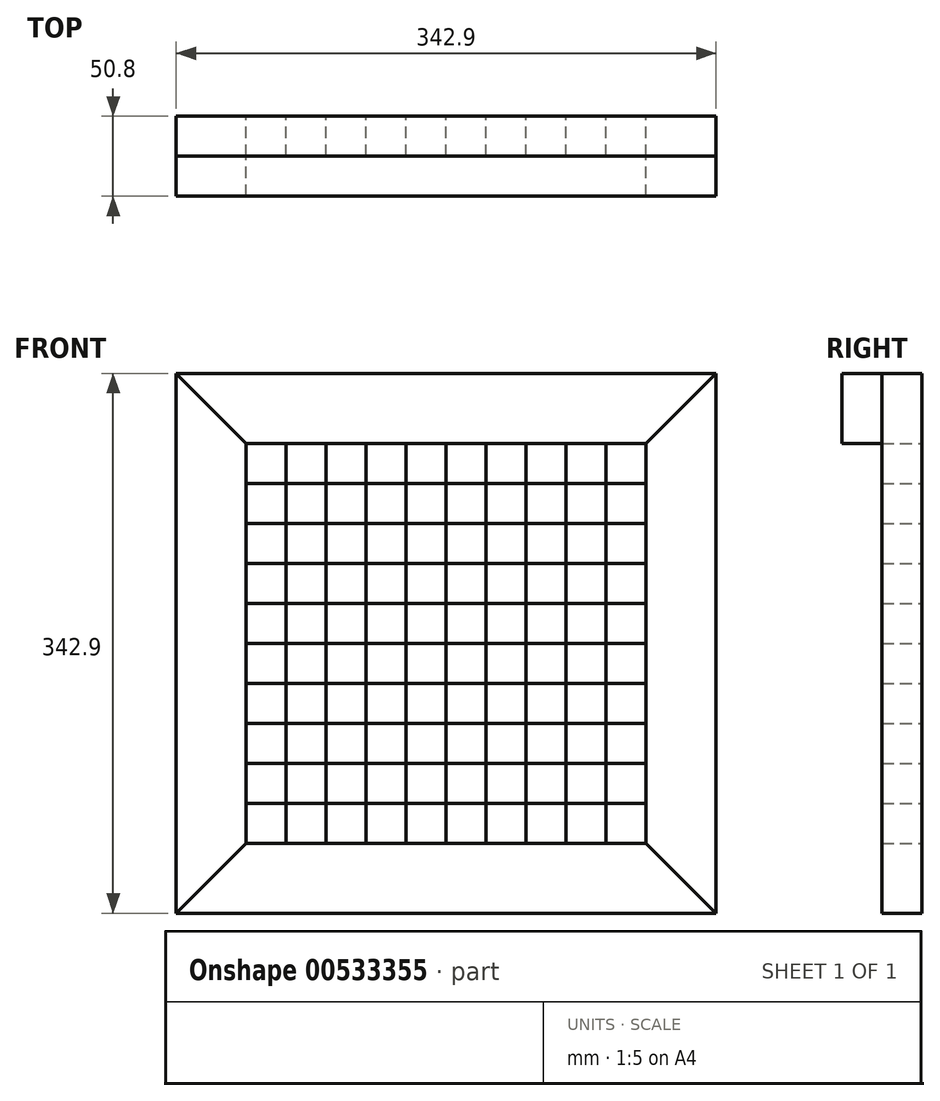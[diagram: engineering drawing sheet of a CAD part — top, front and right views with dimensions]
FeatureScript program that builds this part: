
annotation { "Feature Type Name" : "Feature", "Feature Type Description" : "" }
export const myFeature = defineFeature(function(context is Context, id is Id, definition is map)
    precondition{}
    {
        {
            var Q0;
            Q0=qCreatedBy(makeId("Front.planeOp"),FACE);
            var sketch = newSketch(context, id + "F0", { "sketchPlane" : qUnion([Q0])});
            skLineSegment(sketch, "E0.bottom", {"start": v(171.45, 171.45) * mm, "end": v(-171.45, 171.45) * mm});
            skLineSegment(sketch, "E0.top", {"start": v(171.45, -171.45) * mm, "end": v(-171.45, -171.45) * mm});
            skLineSegment(sketch, "E0.left", {"start": v(171.45, 171.45) * mm, "end": v(171.45, -171.45) * mm});
            skLineSegment(sketch, "E0.right", {"start": v(-171.45, 171.45) * mm, "end": v(-171.45, -171.45) * mm});
            skPoint(sketch, "E0.middle", {"position": v(0, 0) * mm});
            skLineSegment(sketch, "E1", {"start": v(-127, 127) * mm, "end": v(-127, -127) * mm});
            skLineSegment(sketch, "E2", {"start": v(127, 127) * mm, "end": v(127, -127) * mm});
            skLineSegment(sketch, "E3", {"start": v(-127, 127) * mm, "end": v(127, 127) * mm});
            skLineSegment(sketch, "E4", {"start": v(-127, -127) * mm, "end": v(127, -127) * mm});
            skLineSegment(sketch, "E5", {"start": v(-127, 127) * mm, "end": v(-171.45, 171.45) * mm});
            skLineSegment(sketch, "E6", {"start": v(127, 127) * mm, "end": v(171.45, 171.45) * mm});
            skLineSegment(sketch, "E7", {"start": v(127, -127) * mm, "end": v(171.45, -171.45) * mm});
            skLineSegment(sketch, "E8", {"start": v(-127, -127) * mm, "end": v(-171.45, -171.45) * mm});
            skLineSegment(sketch, "E9.0", {"start": v(-101.6, 127) * mm, "end": v(-101.6, -127) * mm});
            skLineSegment(sketch, "E10.0", {"start": v(-76.2, 127) * mm, "end": v(-76.2, -127) * mm});
            skLineSegment(sketch, "E11.0", {"start": v(-50.8, 127) * mm, "end": v(-50.8, -127) * mm});
            skLineSegment(sketch, "E12.0", {"start": v(-25.4, 127) * mm, "end": v(-25.4, -127) * mm});
            skLineSegment(sketch, "E13.0", {"start": v(0, 127) * mm, "end": v(0, -127) * mm});
            skLineSegment(sketch, "E14.0", {"start": v(25.4, 127) * mm, "end": v(25.4, -127) * mm});
            skLineSegment(sketch, "E15.0", {"start": v(50.8, 127) * mm, "end": v(50.8, -127) * mm});
            skLineSegment(sketch, "E16.0", {"start": v(76.2, 127) * mm, "end": v(76.2, -127) * mm});
            skLineSegment(sketch, "E17.0", {"start": v(101.6, 127) * mm, "end": v(101.6, -127) * mm});
            skLineSegment(sketch, "E18.0", {"start": v(-127, 101.6) * mm, "end": v(127, 101.6) * mm});
            skLineSegment(sketch, "E19.0", {"start": v(-127, 76.2) * mm, "end": v(127, 76.2) * mm});
            skLineSegment(sketch, "E20.0", {"start": v(-127, 50.8) * mm, "end": v(127, 50.8) * mm});
            skLineSegment(sketch, "E21.0", {"start": v(-127, 25.4) * mm, "end": v(127, 25.4) * mm});
            skLineSegment(sketch, "E22.0", {"start": v(-127, 0) * mm, "end": v(127, 0) * mm});
            skLineSegment(sketch, "E23.0", {"start": v(-127, -25.4) * mm, "end": v(127, -25.4) * mm});
            skLineSegment(sketch, "E24.0", {"start": v(-127, -50.8) * mm, "end": v(127, -50.8) * mm});
            skLineSegment(sketch, "E25.0", {"start": v(-127, -76.2) * mm, "end": v(127, -76.2) * mm});
            skLineSegment(sketch, "E26.0", {"start": v(-127, -101.6) * mm, "end": v(127, -101.6) * mm});
            skSolve(sketch);
        }
        {
            var Q0;
            Q0=makeQuery(id+"F0.imprint","IMPRINT",FACE,{"disambiguationData":[TD([[makeQuery(id+"F0.imprint","IMPRINT",EDGE,{"derivedFrom":sQuery(id+"F0.wireOp",EDGE,"E0.bottom")}),1.0]])]});
            extrude(context, id + "F1", {"entities" : qUnion([Q0]), "depth" : 25.4 * mm, "offsetDistance" : 25.4 * mm});
        }
        {
            var Q0;
            Q0=makeQuery(id+"F0.imprint","IMPRINT",FACE,{"disambiguationData":[TD([[makeQuery(id+"F0.imprint","IMPRINT",EDGE,{"derivedFrom":sQuery(id+"F0.wireOp",EDGE,"E0.right")}),1.0]])]});
            var Q1;
            Q1=makeQuery(id+"F0.imprint","IMPRINT",FACE,{"disambiguationData":[TD([[makeQuery(id+"F0.imprint","IMPRINT",EDGE,{"derivedFrom":sQuery(id+"F0.wireOp",EDGE,"E0.left")}),-1.0]])]});
            extrude(context, id + "F2", {"entities" : qUnion([Q0, Q1]), "depth" : 25.4 * mm, "offsetDistance" : 25.4 * mm});
        }
        {
            var Q0;
            Q0=makeQuery(id+"F0.imprint","IMPRINT",FACE,{"disambiguationData":[TD([[makeQuery(id+"F0.imprint","IMPRINT",EDGE,{"derivedFrom":sQuery(id+"F0.wireOp",EDGE,"E0.top")}),-1.0]])]});
            var Q1;
            Q1=makeQuery(id+"F1.opExtrude","CAP_FACE",FACE,{"disambiguationData":[OSD([sQuery(id+"F0.wireOp",EDGE,"E0.bottom"),sQuery(id+"F0.wireOp",EDGE,"E3"),sQuery(id+"F0.wireOp",EDGE,"E5"),sQuery(id+"F0.wireOp",EDGE,"E6")])],"isStart":false});
            extrude(context, id + "F3", {"entities" : qUnion([Q0, Q1]), "depth" : 25.4 * mm, "offsetDistance" : 25.4 * mm});
        }
        {
            var Q0;
            {var subQ0=sQuery(id+"F0.wireOp",EDGE,"E3");var subQ5=sQuery(id+"F0.wireOp",EDGE,"E9.0");var subQ6=makeQuery(id+"F0.imprint","INTERSECT",VERTEX,{"derivedFrom":[subQ0,subQ5]});Q0=makeQuery(id+"F0.imprint","IMPRINT",FACE,{"disambiguationData":[TD([[makeQuery(id+"F0.imprint","IMPRINT",EDGE,{"disambiguationData":[TD([[subQ6,-1.0]])],"derivedFrom":subQ5}),-1.0]])]});}
            var Q1;
            {var subQ0=sQuery(id+"F0.wireOp",EDGE,"E10.0");var subQ1=sQuery(id+"F0.wireOp",EDGE,"E3");var subQ2=makeQuery(id+"F0.imprint","INTERSECT",VERTEX,{"derivedFrom":[subQ1,subQ0]});Q1=makeQuery(id+"F0.imprint","IMPRINT",FACE,{"disambiguationData":[TD([[makeQuery(id+"F0.imprint","IMPRINT",EDGE,{"disambiguationData":[TD([[subQ2,-1.0]])],"derivedFrom":subQ1}),-1.0]])]});}
            var Q2;
            {var subQ0=sQuery(id+"F0.wireOp",EDGE,"E12.0");var subQ1=sQuery(id+"F0.wireOp",EDGE,"E3");var subQ2=makeQuery(id+"F0.imprint","INTERSECT",VERTEX,{"derivedFrom":[subQ1,subQ0]});Q2=makeQuery(id+"F0.imprint","IMPRINT",FACE,{"disambiguationData":[TD([[makeQuery(id+"F0.imprint","IMPRINT",EDGE,{"disambiguationData":[TD([[subQ2,-1.0]])],"derivedFrom":subQ1}),-1.0]])]});}
            var Q3;
            {var subQ0=sQuery(id+"F0.wireOp",EDGE,"E14.0");var subQ1=sQuery(id+"F0.wireOp",EDGE,"E3");var subQ2=makeQuery(id+"F0.imprint","INTERSECT",VERTEX,{"derivedFrom":[subQ1,subQ0]});Q3=makeQuery(id+"F0.imprint","IMPRINT",FACE,{"disambiguationData":[TD([[makeQuery(id+"F0.imprint","IMPRINT",EDGE,{"disambiguationData":[TD([[subQ2,-1.0]])],"derivedFrom":subQ1}),-1.0]])]});}
            var Q4;
            {var subQ0=sQuery(id+"F0.wireOp",EDGE,"E16.0");var subQ1=sQuery(id+"F0.wireOp",EDGE,"E3");var subQ2=makeQuery(id+"F0.imprint","INTERSECT",VERTEX,{"derivedFrom":[subQ1,subQ0]});Q4=makeQuery(id+"F0.imprint","IMPRINT",FACE,{"disambiguationData":[TD([[makeQuery(id+"F0.imprint","IMPRINT",EDGE,{"disambiguationData":[TD([[subQ2,-1.0]])],"derivedFrom":subQ1}),-1.0]])]});}
            var Q5;
            {var subQ0=sQuery(id+"F0.wireOp",EDGE,"E18.0");var subQ1=sQuery(id+"F0.wireOp",EDGE,"E9.0");var subQ2=makeQuery(id+"F0.imprint","INTERSECT",VERTEX,{"derivedFrom":[subQ1,subQ0]});Q5=makeQuery(id+"F0.imprint","IMPRINT",FACE,{"disambiguationData":[TD([[makeQuery(id+"F0.imprint","IMPRINT",EDGE,{"disambiguationData":[TD([[subQ2,-1.0]])],"derivedFrom":subQ1}),1.0]])]});}
            var Q6;
            {var subQ0=sQuery(id+"F0.wireOp",EDGE,"E18.0");var subQ1=sQuery(id+"F0.wireOp",EDGE,"E11.0");var subQ2=makeQuery(id+"F0.imprint","INTERSECT",VERTEX,{"derivedFrom":[subQ1,subQ0]});Q6=makeQuery(id+"F0.imprint","IMPRINT",FACE,{"disambiguationData":[TD([[makeQuery(id+"F0.imprint","IMPRINT",EDGE,{"disambiguationData":[TD([[subQ2,-1.0]])],"derivedFrom":subQ1}),1.0]])]});}
            var Q7;
            {var subQ0=sQuery(id+"F0.wireOp",EDGE,"E18.0");var subQ1=sQuery(id+"F0.wireOp",EDGE,"E13.0");var subQ2=makeQuery(id+"F0.imprint","INTERSECT",VERTEX,{"derivedFrom":[subQ1,subQ0]});Q7=makeQuery(id+"F0.imprint","IMPRINT",FACE,{"disambiguationData":[TD([[makeQuery(id+"F0.imprint","IMPRINT",EDGE,{"disambiguationData":[TD([[subQ2,-1.0]])],"derivedFrom":subQ1}),1.0]])]});}
            var Q8;
            {var subQ0=sQuery(id+"F0.wireOp",EDGE,"E18.0");var subQ1=sQuery(id+"F0.wireOp",EDGE,"E15.0");var subQ2=makeQuery(id+"F0.imprint","INTERSECT",VERTEX,{"derivedFrom":[subQ1,subQ0]});Q8=makeQuery(id+"F0.imprint","IMPRINT",FACE,{"disambiguationData":[TD([[makeQuery(id+"F0.imprint","IMPRINT",EDGE,{"disambiguationData":[TD([[subQ2,-1.0]])],"derivedFrom":subQ1}),1.0]])]});}
            var Q9;
            {var subQ0=sQuery(id+"F0.wireOp",EDGE,"E18.0");var subQ1=sQuery(id+"F0.wireOp",EDGE,"E2");var subQ2=makeQuery(id+"F0.imprint","INTERSECT",VERTEX,{"derivedFrom":[subQ1,subQ0]});Q9=makeQuery(id+"F0.imprint","IMPRINT",FACE,{"disambiguationData":[TD([[makeQuery(id+"F0.imprint","IMPRINT",EDGE,{"disambiguationData":[TD([[subQ2,-1.0]])],"derivedFrom":subQ1}),-1.0]])]});}
            var Q10;
            {var subQ0=sQuery(id+"F0.wireOp",EDGE,"E19.0");var subQ1=sQuery(id+"F0.wireOp",EDGE,"E16.0");var subQ2=makeQuery(id+"F0.imprint","INTERSECT",VERTEX,{"derivedFrom":[subQ1,subQ0]});Q10=makeQuery(id+"F0.imprint","IMPRINT",FACE,{"disambiguationData":[TD([[makeQuery(id+"F0.imprint","IMPRINT",EDGE,{"disambiguationData":[TD([[subQ2,-1.0]])],"derivedFrom":subQ1}),1.0]])]});}
            var Q11;
            {var subQ0=sQuery(id+"F0.wireOp",EDGE,"E19.0");var subQ1=sQuery(id+"F0.wireOp",EDGE,"E14.0");var subQ2=makeQuery(id+"F0.imprint","INTERSECT",VERTEX,{"derivedFrom":[subQ1,subQ0]});Q11=makeQuery(id+"F0.imprint","IMPRINT",FACE,{"disambiguationData":[TD([[makeQuery(id+"F0.imprint","IMPRINT",EDGE,{"disambiguationData":[TD([[subQ2,-1.0]])],"derivedFrom":subQ1}),1.0]])]});}
            var Q12;
            {var subQ0=sQuery(id+"F0.wireOp",EDGE,"E19.0");var subQ1=sQuery(id+"F0.wireOp",EDGE,"E12.0");var subQ2=makeQuery(id+"F0.imprint","INTERSECT",VERTEX,{"derivedFrom":[subQ1,subQ0]});Q12=makeQuery(id+"F0.imprint","IMPRINT",FACE,{"disambiguationData":[TD([[makeQuery(id+"F0.imprint","IMPRINT",EDGE,{"disambiguationData":[TD([[subQ2,-1.0]])],"derivedFrom":subQ1}),1.0]])]});}
            var Q13;
            {var subQ0=sQuery(id+"F0.wireOp",EDGE,"E19.0");var subQ1=sQuery(id+"F0.wireOp",EDGE,"E10.0");var subQ2=makeQuery(id+"F0.imprint","INTERSECT",VERTEX,{"derivedFrom":[subQ1,subQ0]});Q13=makeQuery(id+"F0.imprint","IMPRINT",FACE,{"disambiguationData":[TD([[makeQuery(id+"F0.imprint","IMPRINT",EDGE,{"disambiguationData":[TD([[subQ2,-1.0]])],"derivedFrom":subQ1}),1.0]])]});}
            var Q14;
            {var subQ0=sQuery(id+"F0.wireOp",EDGE,"E19.0");var subQ1=sQuery(id+"F0.wireOp",EDGE,"E1");var subQ2=makeQuery(id+"F0.imprint","INTERSECT",VERTEX,{"derivedFrom":[subQ1,subQ0]});Q14=makeQuery(id+"F0.imprint","IMPRINT",FACE,{"disambiguationData":[TD([[makeQuery(id+"F0.imprint","IMPRINT",EDGE,{"disambiguationData":[TD([[subQ2,-1.0]])],"derivedFrom":subQ1}),1.0]])]});}
            var Q15;
            {var subQ0=sQuery(id+"F0.wireOp",EDGE,"E20.0");var subQ1=sQuery(id+"F0.wireOp",EDGE,"E9.0");var subQ2=makeQuery(id+"F0.imprint","INTERSECT",VERTEX,{"derivedFrom":[subQ1,subQ0]});Q15=makeQuery(id+"F0.imprint","IMPRINT",FACE,{"disambiguationData":[TD([[makeQuery(id+"F0.imprint","IMPRINT",EDGE,{"disambiguationData":[TD([[subQ2,-1.0]])],"derivedFrom":subQ1}),1.0]])]});}
            var Q16;
            {var subQ0=sQuery(id+"F0.wireOp",EDGE,"E20.0");var subQ1=sQuery(id+"F0.wireOp",EDGE,"E11.0");var subQ2=makeQuery(id+"F0.imprint","INTERSECT",VERTEX,{"derivedFrom":[subQ1,subQ0]});Q16=makeQuery(id+"F0.imprint","IMPRINT",FACE,{"disambiguationData":[TD([[makeQuery(id+"F0.imprint","IMPRINT",EDGE,{"disambiguationData":[TD([[subQ2,-1.0]])],"derivedFrom":subQ1}),1.0]])]});}
            var Q17;
            {var subQ0=sQuery(id+"F0.wireOp",EDGE,"E20.0");var subQ1=sQuery(id+"F0.wireOp",EDGE,"E13.0");var subQ2=makeQuery(id+"F0.imprint","INTERSECT",VERTEX,{"derivedFrom":[subQ1,subQ0]});Q17=makeQuery(id+"F0.imprint","IMPRINT",FACE,{"disambiguationData":[TD([[makeQuery(id+"F0.imprint","IMPRINT",EDGE,{"disambiguationData":[TD([[subQ2,-1.0]])],"derivedFrom":subQ1}),1.0]])]});}
            var Q18;
            {var subQ0=sQuery(id+"F0.wireOp",EDGE,"E20.0");var subQ1=sQuery(id+"F0.wireOp",EDGE,"E15.0");var subQ2=makeQuery(id+"F0.imprint","INTERSECT",VERTEX,{"derivedFrom":[subQ1,subQ0]});Q18=makeQuery(id+"F0.imprint","IMPRINT",FACE,{"disambiguationData":[TD([[makeQuery(id+"F0.imprint","IMPRINT",EDGE,{"disambiguationData":[TD([[subQ2,-1.0]])],"derivedFrom":subQ1}),1.0]])]});}
            var Q19;
            {var subQ0=sQuery(id+"F0.wireOp",EDGE,"E20.0");var subQ1=sQuery(id+"F0.wireOp",EDGE,"E2");var subQ2=makeQuery(id+"F0.imprint","INTERSECT",VERTEX,{"derivedFrom":[subQ1,subQ0]});Q19=makeQuery(id+"F0.imprint","IMPRINT",FACE,{"disambiguationData":[TD([[makeQuery(id+"F0.imprint","IMPRINT",EDGE,{"disambiguationData":[TD([[subQ2,-1.0]])],"derivedFrom":subQ1}),-1.0]])]});}
            var Q20;
            {var subQ0=sQuery(id+"F0.wireOp",EDGE,"E21.0");var subQ1=sQuery(id+"F0.wireOp",EDGE,"E16.0");var subQ2=makeQuery(id+"F0.imprint","INTERSECT",VERTEX,{"derivedFrom":[subQ1,subQ0]});Q20=makeQuery(id+"F0.imprint","IMPRINT",FACE,{"disambiguationData":[TD([[makeQuery(id+"F0.imprint","IMPRINT",EDGE,{"disambiguationData":[TD([[subQ2,-1.0]])],"derivedFrom":subQ1}),1.0]])]});}
            var Q21;
            {var subQ0=sQuery(id+"F0.wireOp",EDGE,"E21.0");var subQ1=sQuery(id+"F0.wireOp",EDGE,"E14.0");var subQ2=makeQuery(id+"F0.imprint","INTERSECT",VERTEX,{"derivedFrom":[subQ1,subQ0]});Q21=makeQuery(id+"F0.imprint","IMPRINT",FACE,{"disambiguationData":[TD([[makeQuery(id+"F0.imprint","IMPRINT",EDGE,{"disambiguationData":[TD([[subQ2,-1.0]])],"derivedFrom":subQ1}),1.0]])]});}
            var Q22;
            {var subQ0=sQuery(id+"F0.wireOp",EDGE,"E21.0");var subQ1=sQuery(id+"F0.wireOp",EDGE,"E12.0");var subQ2=makeQuery(id+"F0.imprint","INTERSECT",VERTEX,{"derivedFrom":[subQ1,subQ0]});Q22=makeQuery(id+"F0.imprint","IMPRINT",FACE,{"disambiguationData":[TD([[makeQuery(id+"F0.imprint","IMPRINT",EDGE,{"disambiguationData":[TD([[subQ2,-1.0]])],"derivedFrom":subQ1}),1.0]])]});}
            var Q23;
            {var subQ0=sQuery(id+"F0.wireOp",EDGE,"E21.0");var subQ1=sQuery(id+"F0.wireOp",EDGE,"E10.0");var subQ2=makeQuery(id+"F0.imprint","INTERSECT",VERTEX,{"derivedFrom":[subQ1,subQ0]});Q23=makeQuery(id+"F0.imprint","IMPRINT",FACE,{"disambiguationData":[TD([[makeQuery(id+"F0.imprint","IMPRINT",EDGE,{"disambiguationData":[TD([[subQ2,-1.0]])],"derivedFrom":subQ1}),1.0]])]});}
            var Q24;
            {var subQ0=sQuery(id+"F0.wireOp",EDGE,"E21.0");var subQ1=sQuery(id+"F0.wireOp",EDGE,"E1");var subQ2=makeQuery(id+"F0.imprint","INTERSECT",VERTEX,{"derivedFrom":[subQ1,subQ0]});Q24=makeQuery(id+"F0.imprint","IMPRINT",FACE,{"disambiguationData":[TD([[makeQuery(id+"F0.imprint","IMPRINT",EDGE,{"disambiguationData":[TD([[subQ2,-1.0]])],"derivedFrom":subQ1}),1.0]])]});}
            var Q25;
            {var subQ0=sQuery(id+"F0.wireOp",EDGE,"E22.0");var subQ1=sQuery(id+"F0.wireOp",EDGE,"E9.0");var subQ2=makeQuery(id+"F0.imprint","INTERSECT",VERTEX,{"derivedFrom":[subQ1,subQ0]});Q25=makeQuery(id+"F0.imprint","IMPRINT",FACE,{"disambiguationData":[TD([[makeQuery(id+"F0.imprint","IMPRINT",EDGE,{"disambiguationData":[TD([[subQ2,-1.0]])],"derivedFrom":subQ1}),1.0]])]});}
            var Q26;
            {var subQ0=sQuery(id+"F0.wireOp",EDGE,"E22.0");var subQ1=sQuery(id+"F0.wireOp",EDGE,"E11.0");var subQ2=makeQuery(id+"F0.imprint","INTERSECT",VERTEX,{"derivedFrom":[subQ1,subQ0]});Q26=makeQuery(id+"F0.imprint","IMPRINT",FACE,{"disambiguationData":[TD([[makeQuery(id+"F0.imprint","IMPRINT",EDGE,{"disambiguationData":[TD([[subQ2,-1.0]])],"derivedFrom":subQ1}),1.0]])]});}
            var Q27;
            {var subQ0=sQuery(id+"F0.wireOp",EDGE,"E22.0");var subQ1=sQuery(id+"F0.wireOp",EDGE,"E13.0");var subQ2=makeQuery(id+"F0.imprint","INTERSECT",VERTEX,{"derivedFrom":[subQ1,subQ0]});Q27=makeQuery(id+"F0.imprint","IMPRINT",FACE,{"disambiguationData":[TD([[makeQuery(id+"F0.imprint","IMPRINT",EDGE,{"disambiguationData":[TD([[subQ2,-1.0]])],"derivedFrom":subQ1}),1.0]])]});}
            var Q28;
            {var subQ0=sQuery(id+"F0.wireOp",EDGE,"E22.0");var subQ1=sQuery(id+"F0.wireOp",EDGE,"E15.0");var subQ2=makeQuery(id+"F0.imprint","INTERSECT",VERTEX,{"derivedFrom":[subQ1,subQ0]});Q28=makeQuery(id+"F0.imprint","IMPRINT",FACE,{"disambiguationData":[TD([[makeQuery(id+"F0.imprint","IMPRINT",EDGE,{"disambiguationData":[TD([[subQ2,-1.0]])],"derivedFrom":subQ1}),1.0]])]});}
            var Q29;
            {var subQ0=sQuery(id+"F0.wireOp",EDGE,"E22.0");var subQ1=sQuery(id+"F0.wireOp",EDGE,"E2");var subQ2=makeQuery(id+"F0.imprint","INTERSECT",VERTEX,{"derivedFrom":[subQ1,subQ0]});Q29=makeQuery(id+"F0.imprint","IMPRINT",FACE,{"disambiguationData":[TD([[makeQuery(id+"F0.imprint","IMPRINT",EDGE,{"disambiguationData":[TD([[subQ2,-1.0]])],"derivedFrom":subQ1}),-1.0]])]});}
            var Q30;
            {var subQ0=sQuery(id+"F0.wireOp",EDGE,"E23.0");var subQ1=sQuery(id+"F0.wireOp",EDGE,"E16.0");var subQ2=makeQuery(id+"F0.imprint","INTERSECT",VERTEX,{"derivedFrom":[subQ1,subQ0]});Q30=makeQuery(id+"F0.imprint","IMPRINT",FACE,{"disambiguationData":[TD([[makeQuery(id+"F0.imprint","IMPRINT",EDGE,{"disambiguationData":[TD([[subQ2,-1.0]])],"derivedFrom":subQ1}),1.0]])]});}
            var Q31;
            {var subQ0=sQuery(id+"F0.wireOp",EDGE,"E23.0");var subQ1=sQuery(id+"F0.wireOp",EDGE,"E14.0");var subQ2=makeQuery(id+"F0.imprint","INTERSECT",VERTEX,{"derivedFrom":[subQ1,subQ0]});Q31=makeQuery(id+"F0.imprint","IMPRINT",FACE,{"disambiguationData":[TD([[makeQuery(id+"F0.imprint","IMPRINT",EDGE,{"disambiguationData":[TD([[subQ2,-1.0]])],"derivedFrom":subQ1}),1.0]])]});}
            var Q32;
            {var subQ0=sQuery(id+"F0.wireOp",EDGE,"E23.0");var subQ1=sQuery(id+"F0.wireOp",EDGE,"E12.0");var subQ2=makeQuery(id+"F0.imprint","INTERSECT",VERTEX,{"derivedFrom":[subQ1,subQ0]});Q32=makeQuery(id+"F0.imprint","IMPRINT",FACE,{"disambiguationData":[TD([[makeQuery(id+"F0.imprint","IMPRINT",EDGE,{"disambiguationData":[TD([[subQ2,-1.0]])],"derivedFrom":subQ1}),1.0]])]});}
            var Q33;
            {var subQ0=sQuery(id+"F0.wireOp",EDGE,"E23.0");var subQ1=sQuery(id+"F0.wireOp",EDGE,"E10.0");var subQ2=makeQuery(id+"F0.imprint","INTERSECT",VERTEX,{"derivedFrom":[subQ1,subQ0]});Q33=makeQuery(id+"F0.imprint","IMPRINT",FACE,{"disambiguationData":[TD([[makeQuery(id+"F0.imprint","IMPRINT",EDGE,{"disambiguationData":[TD([[subQ2,-1.0]])],"derivedFrom":subQ1}),1.0]])]});}
            var Q34;
            {var subQ0=sQuery(id+"F0.wireOp",EDGE,"E23.0");var subQ1=sQuery(id+"F0.wireOp",EDGE,"E1");var subQ2=makeQuery(id+"F0.imprint","INTERSECT",VERTEX,{"derivedFrom":[subQ1,subQ0]});Q34=makeQuery(id+"F0.imprint","IMPRINT",FACE,{"disambiguationData":[TD([[makeQuery(id+"F0.imprint","IMPRINT",EDGE,{"disambiguationData":[TD([[subQ2,-1.0]])],"derivedFrom":subQ1}),1.0]])]});}
            var Q35;
            {var subQ0=sQuery(id+"F0.wireOp",EDGE,"E24.0");var subQ1=sQuery(id+"F0.wireOp",EDGE,"E9.0");var subQ2=makeQuery(id+"F0.imprint","INTERSECT",VERTEX,{"derivedFrom":[subQ1,subQ0]});Q35=makeQuery(id+"F0.imprint","IMPRINT",FACE,{"disambiguationData":[TD([[makeQuery(id+"F0.imprint","IMPRINT",EDGE,{"disambiguationData":[TD([[subQ2,-1.0]])],"derivedFrom":subQ1}),1.0]])]});}
            var Q36;
            {var subQ0=sQuery(id+"F0.wireOp",EDGE,"E24.0");var subQ1=sQuery(id+"F0.wireOp",EDGE,"E11.0");var subQ2=makeQuery(id+"F0.imprint","INTERSECT",VERTEX,{"derivedFrom":[subQ1,subQ0]});Q36=makeQuery(id+"F0.imprint","IMPRINT",FACE,{"disambiguationData":[TD([[makeQuery(id+"F0.imprint","IMPRINT",EDGE,{"disambiguationData":[TD([[subQ2,-1.0]])],"derivedFrom":subQ1}),1.0]])]});}
            var Q37;
            {var subQ0=sQuery(id+"F0.wireOp",EDGE,"E24.0");var subQ1=sQuery(id+"F0.wireOp",EDGE,"E13.0");var subQ2=makeQuery(id+"F0.imprint","INTERSECT",VERTEX,{"derivedFrom":[subQ1,subQ0]});Q37=makeQuery(id+"F0.imprint","IMPRINT",FACE,{"disambiguationData":[TD([[makeQuery(id+"F0.imprint","IMPRINT",EDGE,{"disambiguationData":[TD([[subQ2,-1.0]])],"derivedFrom":subQ1}),1.0]])]});}
            var Q38;
            {var subQ0=sQuery(id+"F0.wireOp",EDGE,"E24.0");var subQ1=sQuery(id+"F0.wireOp",EDGE,"E15.0");var subQ2=makeQuery(id+"F0.imprint","INTERSECT",VERTEX,{"derivedFrom":[subQ1,subQ0]});Q38=makeQuery(id+"F0.imprint","IMPRINT",FACE,{"disambiguationData":[TD([[makeQuery(id+"F0.imprint","IMPRINT",EDGE,{"disambiguationData":[TD([[subQ2,-1.0]])],"derivedFrom":subQ1}),1.0]])]});}
            var Q39;
            {var subQ0=sQuery(id+"F0.wireOp",EDGE,"E24.0");var subQ1=sQuery(id+"F0.wireOp",EDGE,"E2");var subQ2=makeQuery(id+"F0.imprint","INTERSECT",VERTEX,{"derivedFrom":[subQ1,subQ0]});Q39=makeQuery(id+"F0.imprint","IMPRINT",FACE,{"disambiguationData":[TD([[makeQuery(id+"F0.imprint","IMPRINT",EDGE,{"disambiguationData":[TD([[subQ2,-1.0]])],"derivedFrom":subQ1}),-1.0]])]});}
            var Q40;
            {var subQ0=sQuery(id+"F0.wireOp",EDGE,"E25.0");var subQ1=sQuery(id+"F0.wireOp",EDGE,"E16.0");var subQ2=makeQuery(id+"F0.imprint","INTERSECT",VERTEX,{"derivedFrom":[subQ1,subQ0]});Q40=makeQuery(id+"F0.imprint","IMPRINT",FACE,{"disambiguationData":[TD([[makeQuery(id+"F0.imprint","IMPRINT",EDGE,{"disambiguationData":[TD([[subQ2,-1.0]])],"derivedFrom":subQ1}),1.0]])]});}
            var Q41;
            {var subQ0=sQuery(id+"F0.wireOp",EDGE,"E25.0");var subQ1=sQuery(id+"F0.wireOp",EDGE,"E14.0");var subQ2=makeQuery(id+"F0.imprint","INTERSECT",VERTEX,{"derivedFrom":[subQ1,subQ0]});Q41=makeQuery(id+"F0.imprint","IMPRINT",FACE,{"disambiguationData":[TD([[makeQuery(id+"F0.imprint","IMPRINT",EDGE,{"disambiguationData":[TD([[subQ2,-1.0]])],"derivedFrom":subQ1}),1.0]])]});}
            var Q42;
            {var subQ0=sQuery(id+"F0.wireOp",EDGE,"E25.0");var subQ1=sQuery(id+"F0.wireOp",EDGE,"E12.0");var subQ2=makeQuery(id+"F0.imprint","INTERSECT",VERTEX,{"derivedFrom":[subQ1,subQ0]});Q42=makeQuery(id+"F0.imprint","IMPRINT",FACE,{"disambiguationData":[TD([[makeQuery(id+"F0.imprint","IMPRINT",EDGE,{"disambiguationData":[TD([[subQ2,-1.0]])],"derivedFrom":subQ1}),1.0]])]});}
            var Q43;
            {var subQ0=sQuery(id+"F0.wireOp",EDGE,"E25.0");var subQ1=sQuery(id+"F0.wireOp",EDGE,"E10.0");var subQ2=makeQuery(id+"F0.imprint","INTERSECT",VERTEX,{"derivedFrom":[subQ1,subQ0]});Q43=makeQuery(id+"F0.imprint","IMPRINT",FACE,{"disambiguationData":[TD([[makeQuery(id+"F0.imprint","IMPRINT",EDGE,{"disambiguationData":[TD([[subQ2,-1.0]])],"derivedFrom":subQ1}),1.0]])]});}
            var Q44;
            {var subQ0=sQuery(id+"F0.wireOp",EDGE,"E25.0");var subQ1=sQuery(id+"F0.wireOp",EDGE,"E1");var subQ2=makeQuery(id+"F0.imprint","INTERSECT",VERTEX,{"derivedFrom":[subQ1,subQ0]});Q44=makeQuery(id+"F0.imprint","IMPRINT",FACE,{"disambiguationData":[TD([[makeQuery(id+"F0.imprint","IMPRINT",EDGE,{"disambiguationData":[TD([[subQ2,-1.0]])],"derivedFrom":subQ1}),1.0]])]});}
            var Q45;
            {var subQ0=sQuery(id+"F0.wireOp",EDGE,"E9.0");var subQ1=sQuery(id+"F0.wireOp",EDGE,"E4");var subQ2=makeQuery(id+"F0.imprint","INTERSECT",VERTEX,{"derivedFrom":[subQ1,subQ0]});Q45=makeQuery(id+"F0.imprint","IMPRINT",FACE,{"disambiguationData":[TD([[makeQuery(id+"F0.imprint","IMPRINT",EDGE,{"disambiguationData":[TD([[subQ2,-1.0]])],"derivedFrom":subQ1}),1.0]])]});}
            var Q46;
            {var subQ0=sQuery(id+"F0.wireOp",EDGE,"E13.0");var subQ1=sQuery(id+"F0.wireOp",EDGE,"E4");var subQ2=makeQuery(id+"F0.imprint","INTERSECT",VERTEX,{"derivedFrom":[subQ1,subQ0]});Q46=makeQuery(id+"F0.imprint","IMPRINT",FACE,{"disambiguationData":[TD([[makeQuery(id+"F0.imprint","IMPRINT",EDGE,{"disambiguationData":[TD([[subQ2,-1.0]])],"derivedFrom":subQ1}),1.0]])]});}
            var Q47;
            {var subQ0=sQuery(id+"F0.wireOp",EDGE,"E11.0");var subQ1=sQuery(id+"F0.wireOp",EDGE,"E4");var subQ2=makeQuery(id+"F0.imprint","INTERSECT",VERTEX,{"derivedFrom":[subQ1,subQ0]});Q47=makeQuery(id+"F0.imprint","IMPRINT",FACE,{"disambiguationData":[TD([[makeQuery(id+"F0.imprint","IMPRINT",EDGE,{"disambiguationData":[TD([[subQ2,-1.0]])],"derivedFrom":subQ1}),1.0]])]});}
            var Q48;
            {var subQ0=sQuery(id+"F0.wireOp",EDGE,"E15.0");var subQ1=sQuery(id+"F0.wireOp",EDGE,"E4");var subQ2=makeQuery(id+"F0.imprint","INTERSECT",VERTEX,{"derivedFrom":[subQ1,subQ0]});Q48=makeQuery(id+"F0.imprint","IMPRINT",FACE,{"disambiguationData":[TD([[makeQuery(id+"F0.imprint","IMPRINT",EDGE,{"disambiguationData":[TD([[subQ2,-1.0]])],"derivedFrom":subQ1}),1.0]])]});}
            var Q49;
            {var subQ0=sQuery(id+"F0.wireOp",EDGE,"E4");var subQ5=sQuery(id+"F0.wireOp",EDGE,"E17.0");var subQ6=makeQuery(id+"F0.imprint","INTERSECT",VERTEX,{"derivedFrom":[subQ0,subQ5]});Q49=makeQuery(id+"F0.imprint","IMPRINT",FACE,{"disambiguationData":[TD([[makeQuery(id+"F0.imprint","IMPRINT",EDGE,{"disambiguationData":[TD([[subQ6,1.0]])],"derivedFrom":subQ5}),1.0]])]});}
            extrude(context, id + "F4", {"entities" : qUnion([Q0, Q1, Q2, Q3, Q4, Q5, Q6, Q7, Q8, Q9, Q10, Q11, Q12, Q13, Q14, Q15, Q16, Q17, Q18, Q19, Q20, Q21, Q22, Q23, Q24, Q25, Q26, Q27, Q28, Q29, Q30, Q31, Q32, Q33, Q34, Q35, Q36, Q37, Q38, Q39, Q40, Q41, Q42, Q43, Q44, Q45, Q46, Q47, Q48, Q49]), "depth" : 25.4 * mm, "offsetDistance" : 25.4 * mm});
        }
        {
            var Q0;
            {var subQ0=sQuery(id+"F0.wireOp",EDGE,"E9.0");var subQ1=sQuery(id+"F0.wireOp",EDGE,"E3");var subQ2=makeQuery(id+"F0.imprint","INTERSECT",VERTEX,{"derivedFrom":[subQ1,subQ0]});Q0=makeQuery(id+"F0.imprint","IMPRINT",FACE,{"disambiguationData":[TD([[makeQuery(id+"F0.imprint","IMPRINT",EDGE,{"disambiguationData":[TD([[subQ2,-1.0]])],"derivedFrom":subQ1}),-1.0]])]});}
            var Q1;
            {var subQ0=sQuery(id+"F0.wireOp",EDGE,"E11.0");var subQ1=sQuery(id+"F0.wireOp",EDGE,"E3");var subQ2=makeQuery(id+"F0.imprint","INTERSECT",VERTEX,{"derivedFrom":[subQ1,subQ0]});Q1=makeQuery(id+"F0.imprint","IMPRINT",FACE,{"disambiguationData":[TD([[makeQuery(id+"F0.imprint","IMPRINT",EDGE,{"disambiguationData":[TD([[subQ2,-1.0]])],"derivedFrom":subQ1}),-1.0]])]});}
            var Q2;
            {var subQ0=sQuery(id+"F0.wireOp",EDGE,"E13.0");var subQ1=sQuery(id+"F0.wireOp",EDGE,"E3");var subQ2=makeQuery(id+"F0.imprint","INTERSECT",VERTEX,{"derivedFrom":[subQ1,subQ0]});Q2=makeQuery(id+"F0.imprint","IMPRINT",FACE,{"disambiguationData":[TD([[makeQuery(id+"F0.imprint","IMPRINT",EDGE,{"disambiguationData":[TD([[subQ2,-1.0]])],"derivedFrom":subQ1}),-1.0]])]});}
            var Q3;
            {var subQ0=sQuery(id+"F0.wireOp",EDGE,"E15.0");var subQ1=sQuery(id+"F0.wireOp",EDGE,"E3");var subQ2=makeQuery(id+"F0.imprint","INTERSECT",VERTEX,{"derivedFrom":[subQ1,subQ0]});Q3=makeQuery(id+"F0.imprint","IMPRINT",FACE,{"disambiguationData":[TD([[makeQuery(id+"F0.imprint","IMPRINT",EDGE,{"disambiguationData":[TD([[subQ2,-1.0]])],"derivedFrom":subQ1}),-1.0]])]});}
            var Q4;
            {var subQ0=sQuery(id+"F0.wireOp",EDGE,"E3");var subQ5=sQuery(id+"F0.wireOp",EDGE,"E17.0");var subQ6=makeQuery(id+"F0.imprint","INTERSECT",VERTEX,{"derivedFrom":[subQ0,subQ5]});Q4=makeQuery(id+"F0.imprint","IMPRINT",FACE,{"disambiguationData":[TD([[makeQuery(id+"F0.imprint","IMPRINT",EDGE,{"disambiguationData":[TD([[subQ6,-1.0]])],"derivedFrom":subQ5}),1.0]])]});}
            var Q5;
            {var subQ0=sQuery(id+"F0.wireOp",EDGE,"E18.0");var subQ1=sQuery(id+"F0.wireOp",EDGE,"E16.0");var subQ2=makeQuery(id+"F0.imprint","INTERSECT",VERTEX,{"derivedFrom":[subQ1,subQ0]});Q5=makeQuery(id+"F0.imprint","IMPRINT",FACE,{"disambiguationData":[TD([[makeQuery(id+"F0.imprint","IMPRINT",EDGE,{"disambiguationData":[TD([[subQ2,-1.0]])],"derivedFrom":subQ1}),1.0]])]});}
            var Q6;
            {var subQ0=sQuery(id+"F0.wireOp",EDGE,"E18.0");var subQ1=sQuery(id+"F0.wireOp",EDGE,"E14.0");var subQ2=makeQuery(id+"F0.imprint","INTERSECT",VERTEX,{"derivedFrom":[subQ1,subQ0]});Q6=makeQuery(id+"F0.imprint","IMPRINT",FACE,{"disambiguationData":[TD([[makeQuery(id+"F0.imprint","IMPRINT",EDGE,{"disambiguationData":[TD([[subQ2,-1.0]])],"derivedFrom":subQ1}),1.0]])]});}
            var Q7;
            {var subQ0=sQuery(id+"F0.wireOp",EDGE,"E18.0");var subQ1=sQuery(id+"F0.wireOp",EDGE,"E12.0");var subQ2=makeQuery(id+"F0.imprint","INTERSECT",VERTEX,{"derivedFrom":[subQ1,subQ0]});Q7=makeQuery(id+"F0.imprint","IMPRINT",FACE,{"disambiguationData":[TD([[makeQuery(id+"F0.imprint","IMPRINT",EDGE,{"disambiguationData":[TD([[subQ2,-1.0]])],"derivedFrom":subQ1}),1.0]])]});}
            var Q8;
            {var subQ0=sQuery(id+"F0.wireOp",EDGE,"E18.0");var subQ1=sQuery(id+"F0.wireOp",EDGE,"E10.0");var subQ2=makeQuery(id+"F0.imprint","INTERSECT",VERTEX,{"derivedFrom":[subQ1,subQ0]});Q8=makeQuery(id+"F0.imprint","IMPRINT",FACE,{"disambiguationData":[TD([[makeQuery(id+"F0.imprint","IMPRINT",EDGE,{"disambiguationData":[TD([[subQ2,-1.0]])],"derivedFrom":subQ1}),1.0]])]});}
            var Q9;
            {var subQ0=sQuery(id+"F0.wireOp",EDGE,"E18.0");var subQ1=sQuery(id+"F0.wireOp",EDGE,"E1");var subQ2=makeQuery(id+"F0.imprint","INTERSECT",VERTEX,{"derivedFrom":[subQ1,subQ0]});Q9=makeQuery(id+"F0.imprint","IMPRINT",FACE,{"disambiguationData":[TD([[makeQuery(id+"F0.imprint","IMPRINT",EDGE,{"disambiguationData":[TD([[subQ2,-1.0]])],"derivedFrom":subQ1}),1.0]])]});}
            var Q10;
            {var subQ0=sQuery(id+"F0.wireOp",EDGE,"E19.0");var subQ1=sQuery(id+"F0.wireOp",EDGE,"E9.0");var subQ2=makeQuery(id+"F0.imprint","INTERSECT",VERTEX,{"derivedFrom":[subQ1,subQ0]});Q10=makeQuery(id+"F0.imprint","IMPRINT",FACE,{"disambiguationData":[TD([[makeQuery(id+"F0.imprint","IMPRINT",EDGE,{"disambiguationData":[TD([[subQ2,-1.0]])],"derivedFrom":subQ1}),1.0]])]});}
            var Q11;
            {var subQ0=sQuery(id+"F0.wireOp",EDGE,"E19.0");var subQ1=sQuery(id+"F0.wireOp",EDGE,"E11.0");var subQ2=makeQuery(id+"F0.imprint","INTERSECT",VERTEX,{"derivedFrom":[subQ1,subQ0]});Q11=makeQuery(id+"F0.imprint","IMPRINT",FACE,{"disambiguationData":[TD([[makeQuery(id+"F0.imprint","IMPRINT",EDGE,{"disambiguationData":[TD([[subQ2,-1.0]])],"derivedFrom":subQ1}),1.0]])]});}
            var Q12;
            {var subQ0=sQuery(id+"F0.wireOp",EDGE,"E19.0");var subQ1=sQuery(id+"F0.wireOp",EDGE,"E13.0");var subQ2=makeQuery(id+"F0.imprint","INTERSECT",VERTEX,{"derivedFrom":[subQ1,subQ0]});Q12=makeQuery(id+"F0.imprint","IMPRINT",FACE,{"disambiguationData":[TD([[makeQuery(id+"F0.imprint","IMPRINT",EDGE,{"disambiguationData":[TD([[subQ2,-1.0]])],"derivedFrom":subQ1}),1.0]])]});}
            var Q13;
            {var subQ0=sQuery(id+"F0.wireOp",EDGE,"E19.0");var subQ1=sQuery(id+"F0.wireOp",EDGE,"E15.0");var subQ2=makeQuery(id+"F0.imprint","INTERSECT",VERTEX,{"derivedFrom":[subQ1,subQ0]});Q13=makeQuery(id+"F0.imprint","IMPRINT",FACE,{"disambiguationData":[TD([[makeQuery(id+"F0.imprint","IMPRINT",EDGE,{"disambiguationData":[TD([[subQ2,-1.0]])],"derivedFrom":subQ1}),1.0]])]});}
            var Q14;
            {var subQ0=sQuery(id+"F0.wireOp",EDGE,"E19.0");var subQ1=sQuery(id+"F0.wireOp",EDGE,"E2");var subQ2=makeQuery(id+"F0.imprint","INTERSECT",VERTEX,{"derivedFrom":[subQ1,subQ0]});Q14=makeQuery(id+"F0.imprint","IMPRINT",FACE,{"disambiguationData":[TD([[makeQuery(id+"F0.imprint","IMPRINT",EDGE,{"disambiguationData":[TD([[subQ2,-1.0]])],"derivedFrom":subQ1}),-1.0]])]});}
            var Q15;
            {var subQ0=sQuery(id+"F0.wireOp",EDGE,"E20.0");var subQ1=sQuery(id+"F0.wireOp",EDGE,"E16.0");var subQ2=makeQuery(id+"F0.imprint","INTERSECT",VERTEX,{"derivedFrom":[subQ1,subQ0]});Q15=makeQuery(id+"F0.imprint","IMPRINT",FACE,{"disambiguationData":[TD([[makeQuery(id+"F0.imprint","IMPRINT",EDGE,{"disambiguationData":[TD([[subQ2,-1.0]])],"derivedFrom":subQ1}),1.0]])]});}
            var Q16;
            {var subQ0=sQuery(id+"F0.wireOp",EDGE,"E20.0");var subQ1=sQuery(id+"F0.wireOp",EDGE,"E14.0");var subQ2=makeQuery(id+"F0.imprint","INTERSECT",VERTEX,{"derivedFrom":[subQ1,subQ0]});Q16=makeQuery(id+"F0.imprint","IMPRINT",FACE,{"disambiguationData":[TD([[makeQuery(id+"F0.imprint","IMPRINT",EDGE,{"disambiguationData":[TD([[subQ2,-1.0]])],"derivedFrom":subQ1}),1.0]])]});}
            var Q17;
            {var subQ0=sQuery(id+"F0.wireOp",EDGE,"E20.0");var subQ1=sQuery(id+"F0.wireOp",EDGE,"E12.0");var subQ2=makeQuery(id+"F0.imprint","INTERSECT",VERTEX,{"derivedFrom":[subQ1,subQ0]});Q17=makeQuery(id+"F0.imprint","IMPRINT",FACE,{"disambiguationData":[TD([[makeQuery(id+"F0.imprint","IMPRINT",EDGE,{"disambiguationData":[TD([[subQ2,-1.0]])],"derivedFrom":subQ1}),1.0]])]});}
            var Q18;
            {var subQ0=sQuery(id+"F0.wireOp",EDGE,"E20.0");var subQ1=sQuery(id+"F0.wireOp",EDGE,"E10.0");var subQ2=makeQuery(id+"F0.imprint","INTERSECT",VERTEX,{"derivedFrom":[subQ1,subQ0]});Q18=makeQuery(id+"F0.imprint","IMPRINT",FACE,{"disambiguationData":[TD([[makeQuery(id+"F0.imprint","IMPRINT",EDGE,{"disambiguationData":[TD([[subQ2,-1.0]])],"derivedFrom":subQ1}),1.0]])]});}
            var Q19;
            {var subQ0=sQuery(id+"F0.wireOp",EDGE,"E20.0");var subQ1=sQuery(id+"F0.wireOp",EDGE,"E1");var subQ2=makeQuery(id+"F0.imprint","INTERSECT",VERTEX,{"derivedFrom":[subQ1,subQ0]});Q19=makeQuery(id+"F0.imprint","IMPRINT",FACE,{"disambiguationData":[TD([[makeQuery(id+"F0.imprint","IMPRINT",EDGE,{"disambiguationData":[TD([[subQ2,-1.0]])],"derivedFrom":subQ1}),1.0]])]});}
            var Q20;
            {var subQ0=sQuery(id+"F0.wireOp",EDGE,"E21.0");var subQ1=sQuery(id+"F0.wireOp",EDGE,"E9.0");var subQ2=makeQuery(id+"F0.imprint","INTERSECT",VERTEX,{"derivedFrom":[subQ1,subQ0]});Q20=makeQuery(id+"F0.imprint","IMPRINT",FACE,{"disambiguationData":[TD([[makeQuery(id+"F0.imprint","IMPRINT",EDGE,{"disambiguationData":[TD([[subQ2,-1.0]])],"derivedFrom":subQ1}),1.0]])]});}
            var Q21;
            {var subQ0=sQuery(id+"F0.wireOp",EDGE,"E21.0");var subQ1=sQuery(id+"F0.wireOp",EDGE,"E11.0");var subQ2=makeQuery(id+"F0.imprint","INTERSECT",VERTEX,{"derivedFrom":[subQ1,subQ0]});Q21=makeQuery(id+"F0.imprint","IMPRINT",FACE,{"disambiguationData":[TD([[makeQuery(id+"F0.imprint","IMPRINT",EDGE,{"disambiguationData":[TD([[subQ2,-1.0]])],"derivedFrom":subQ1}),1.0]])]});}
            var Q22;
            {var subQ0=sQuery(id+"F0.wireOp",EDGE,"E21.0");var subQ1=sQuery(id+"F0.wireOp",EDGE,"E13.0");var subQ2=makeQuery(id+"F0.imprint","INTERSECT",VERTEX,{"derivedFrom":[subQ1,subQ0]});Q22=makeQuery(id+"F0.imprint","IMPRINT",FACE,{"disambiguationData":[TD([[makeQuery(id+"F0.imprint","IMPRINT",EDGE,{"disambiguationData":[TD([[subQ2,-1.0]])],"derivedFrom":subQ1}),1.0]])]});}
            var Q23;
            {var subQ0=sQuery(id+"F0.wireOp",EDGE,"E21.0");var subQ1=sQuery(id+"F0.wireOp",EDGE,"E15.0");var subQ2=makeQuery(id+"F0.imprint","INTERSECT",VERTEX,{"derivedFrom":[subQ1,subQ0]});Q23=makeQuery(id+"F0.imprint","IMPRINT",FACE,{"disambiguationData":[TD([[makeQuery(id+"F0.imprint","IMPRINT",EDGE,{"disambiguationData":[TD([[subQ2,-1.0]])],"derivedFrom":subQ1}),1.0]])]});}
            var Q24;
            {var subQ0=sQuery(id+"F0.wireOp",EDGE,"E21.0");var subQ1=sQuery(id+"F0.wireOp",EDGE,"E2");var subQ2=makeQuery(id+"F0.imprint","INTERSECT",VERTEX,{"derivedFrom":[subQ1,subQ0]});Q24=makeQuery(id+"F0.imprint","IMPRINT",FACE,{"disambiguationData":[TD([[makeQuery(id+"F0.imprint","IMPRINT",EDGE,{"disambiguationData":[TD([[subQ2,-1.0]])],"derivedFrom":subQ1}),-1.0]])]});}
            var Q25;
            {var subQ0=sQuery(id+"F0.wireOp",EDGE,"E22.0");var subQ1=sQuery(id+"F0.wireOp",EDGE,"E16.0");var subQ2=makeQuery(id+"F0.imprint","INTERSECT",VERTEX,{"derivedFrom":[subQ1,subQ0]});Q25=makeQuery(id+"F0.imprint","IMPRINT",FACE,{"disambiguationData":[TD([[makeQuery(id+"F0.imprint","IMPRINT",EDGE,{"disambiguationData":[TD([[subQ2,-1.0]])],"derivedFrom":subQ1}),1.0]])]});}
            var Q26;
            {var subQ0=sQuery(id+"F0.wireOp",EDGE,"E22.0");var subQ1=sQuery(id+"F0.wireOp",EDGE,"E14.0");var subQ2=makeQuery(id+"F0.imprint","INTERSECT",VERTEX,{"derivedFrom":[subQ1,subQ0]});Q26=makeQuery(id+"F0.imprint","IMPRINT",FACE,{"disambiguationData":[TD([[makeQuery(id+"F0.imprint","IMPRINT",EDGE,{"disambiguationData":[TD([[subQ2,-1.0]])],"derivedFrom":subQ1}),1.0]])]});}
            var Q27;
            {var subQ0=sQuery(id+"F0.wireOp",EDGE,"E22.0");var subQ1=sQuery(id+"F0.wireOp",EDGE,"E12.0");var subQ2=makeQuery(id+"F0.imprint","INTERSECT",VERTEX,{"derivedFrom":[subQ1,subQ0]});Q27=makeQuery(id+"F0.imprint","IMPRINT",FACE,{"disambiguationData":[TD([[makeQuery(id+"F0.imprint","IMPRINT",EDGE,{"disambiguationData":[TD([[subQ2,-1.0]])],"derivedFrom":subQ1}),1.0]])]});}
            var Q28;
            {var subQ0=sQuery(id+"F0.wireOp",EDGE,"E22.0");var subQ1=sQuery(id+"F0.wireOp",EDGE,"E10.0");var subQ2=makeQuery(id+"F0.imprint","INTERSECT",VERTEX,{"derivedFrom":[subQ1,subQ0]});Q28=makeQuery(id+"F0.imprint","IMPRINT",FACE,{"disambiguationData":[TD([[makeQuery(id+"F0.imprint","IMPRINT",EDGE,{"disambiguationData":[TD([[subQ2,-1.0]])],"derivedFrom":subQ1}),1.0]])]});}
            var Q29;
            {var subQ0=sQuery(id+"F0.wireOp",EDGE,"E22.0");var subQ1=sQuery(id+"F0.wireOp",EDGE,"E1");var subQ2=makeQuery(id+"F0.imprint","INTERSECT",VERTEX,{"derivedFrom":[subQ1,subQ0]});Q29=makeQuery(id+"F0.imprint","IMPRINT",FACE,{"disambiguationData":[TD([[makeQuery(id+"F0.imprint","IMPRINT",EDGE,{"disambiguationData":[TD([[subQ2,-1.0]])],"derivedFrom":subQ1}),1.0]])]});}
            var Q30;
            {var subQ0=sQuery(id+"F0.wireOp",EDGE,"E23.0");var subQ1=sQuery(id+"F0.wireOp",EDGE,"E9.0");var subQ2=makeQuery(id+"F0.imprint","INTERSECT",VERTEX,{"derivedFrom":[subQ1,subQ0]});Q30=makeQuery(id+"F0.imprint","IMPRINT",FACE,{"disambiguationData":[TD([[makeQuery(id+"F0.imprint","IMPRINT",EDGE,{"disambiguationData":[TD([[subQ2,-1.0]])],"derivedFrom":subQ1}),1.0]])]});}
            var Q31;
            {var subQ0=sQuery(id+"F0.wireOp",EDGE,"E23.0");var subQ1=sQuery(id+"F0.wireOp",EDGE,"E11.0");var subQ2=makeQuery(id+"F0.imprint","INTERSECT",VERTEX,{"derivedFrom":[subQ1,subQ0]});Q31=makeQuery(id+"F0.imprint","IMPRINT",FACE,{"disambiguationData":[TD([[makeQuery(id+"F0.imprint","IMPRINT",EDGE,{"disambiguationData":[TD([[subQ2,-1.0]])],"derivedFrom":subQ1}),1.0]])]});}
            var Q32;
            {var subQ0=sQuery(id+"F0.wireOp",EDGE,"E23.0");var subQ1=sQuery(id+"F0.wireOp",EDGE,"E13.0");var subQ2=makeQuery(id+"F0.imprint","INTERSECT",VERTEX,{"derivedFrom":[subQ1,subQ0]});Q32=makeQuery(id+"F0.imprint","IMPRINT",FACE,{"disambiguationData":[TD([[makeQuery(id+"F0.imprint","IMPRINT",EDGE,{"disambiguationData":[TD([[subQ2,-1.0]])],"derivedFrom":subQ1}),1.0]])]});}
            var Q33;
            {var subQ0=sQuery(id+"F0.wireOp",EDGE,"E23.0");var subQ1=sQuery(id+"F0.wireOp",EDGE,"E15.0");var subQ2=makeQuery(id+"F0.imprint","INTERSECT",VERTEX,{"derivedFrom":[subQ1,subQ0]});Q33=makeQuery(id+"F0.imprint","IMPRINT",FACE,{"disambiguationData":[TD([[makeQuery(id+"F0.imprint","IMPRINT",EDGE,{"disambiguationData":[TD([[subQ2,-1.0]])],"derivedFrom":subQ1}),1.0]])]});}
            var Q34;
            {var subQ0=sQuery(id+"F0.wireOp",EDGE,"E23.0");var subQ1=sQuery(id+"F0.wireOp",EDGE,"E2");var subQ2=makeQuery(id+"F0.imprint","INTERSECT",VERTEX,{"derivedFrom":[subQ1,subQ0]});Q34=makeQuery(id+"F0.imprint","IMPRINT",FACE,{"disambiguationData":[TD([[makeQuery(id+"F0.imprint","IMPRINT",EDGE,{"disambiguationData":[TD([[subQ2,-1.0]])],"derivedFrom":subQ1}),-1.0]])]});}
            var Q35;
            {var subQ0=sQuery(id+"F0.wireOp",EDGE,"E24.0");var subQ1=sQuery(id+"F0.wireOp",EDGE,"E16.0");var subQ2=makeQuery(id+"F0.imprint","INTERSECT",VERTEX,{"derivedFrom":[subQ1,subQ0]});Q35=makeQuery(id+"F0.imprint","IMPRINT",FACE,{"disambiguationData":[TD([[makeQuery(id+"F0.imprint","IMPRINT",EDGE,{"disambiguationData":[TD([[subQ2,-1.0]])],"derivedFrom":subQ1}),1.0]])]});}
            var Q36;
            {var subQ0=sQuery(id+"F0.wireOp",EDGE,"E24.0");var subQ1=sQuery(id+"F0.wireOp",EDGE,"E14.0");var subQ2=makeQuery(id+"F0.imprint","INTERSECT",VERTEX,{"derivedFrom":[subQ1,subQ0]});Q36=makeQuery(id+"F0.imprint","IMPRINT",FACE,{"disambiguationData":[TD([[makeQuery(id+"F0.imprint","IMPRINT",EDGE,{"disambiguationData":[TD([[subQ2,-1.0]])],"derivedFrom":subQ1}),1.0]])]});}
            var Q37;
            {var subQ0=sQuery(id+"F0.wireOp",EDGE,"E24.0");var subQ1=sQuery(id+"F0.wireOp",EDGE,"E12.0");var subQ2=makeQuery(id+"F0.imprint","INTERSECT",VERTEX,{"derivedFrom":[subQ1,subQ0]});Q37=makeQuery(id+"F0.imprint","IMPRINT",FACE,{"disambiguationData":[TD([[makeQuery(id+"F0.imprint","IMPRINT",EDGE,{"disambiguationData":[TD([[subQ2,-1.0]])],"derivedFrom":subQ1}),1.0]])]});}
            var Q38;
            {var subQ0=sQuery(id+"F0.wireOp",EDGE,"E24.0");var subQ1=sQuery(id+"F0.wireOp",EDGE,"E10.0");var subQ2=makeQuery(id+"F0.imprint","INTERSECT",VERTEX,{"derivedFrom":[subQ1,subQ0]});Q38=makeQuery(id+"F0.imprint","IMPRINT",FACE,{"disambiguationData":[TD([[makeQuery(id+"F0.imprint","IMPRINT",EDGE,{"disambiguationData":[TD([[subQ2,-1.0]])],"derivedFrom":subQ1}),1.0]])]});}
            var Q39;
            {var subQ0=sQuery(id+"F0.wireOp",EDGE,"E24.0");var subQ1=sQuery(id+"F0.wireOp",EDGE,"E1");var subQ2=makeQuery(id+"F0.imprint","INTERSECT",VERTEX,{"derivedFrom":[subQ1,subQ0]});Q39=makeQuery(id+"F0.imprint","IMPRINT",FACE,{"disambiguationData":[TD([[makeQuery(id+"F0.imprint","IMPRINT",EDGE,{"disambiguationData":[TD([[subQ2,-1.0]])],"derivedFrom":subQ1}),1.0]])]});}
            var Q40;
            {var subQ0=sQuery(id+"F0.wireOp",EDGE,"E25.0");var subQ1=sQuery(id+"F0.wireOp",EDGE,"E9.0");var subQ2=makeQuery(id+"F0.imprint","INTERSECT",VERTEX,{"derivedFrom":[subQ1,subQ0]});Q40=makeQuery(id+"F0.imprint","IMPRINT",FACE,{"disambiguationData":[TD([[makeQuery(id+"F0.imprint","IMPRINT",EDGE,{"disambiguationData":[TD([[subQ2,-1.0]])],"derivedFrom":subQ1}),1.0]])]});}
            var Q41;
            {var subQ0=sQuery(id+"F0.wireOp",EDGE,"E25.0");var subQ1=sQuery(id+"F0.wireOp",EDGE,"E11.0");var subQ2=makeQuery(id+"F0.imprint","INTERSECT",VERTEX,{"derivedFrom":[subQ1,subQ0]});Q41=makeQuery(id+"F0.imprint","IMPRINT",FACE,{"disambiguationData":[TD([[makeQuery(id+"F0.imprint","IMPRINT",EDGE,{"disambiguationData":[TD([[subQ2,-1.0]])],"derivedFrom":subQ1}),1.0]])]});}
            var Q42;
            {var subQ0=sQuery(id+"F0.wireOp",EDGE,"E25.0");var subQ1=sQuery(id+"F0.wireOp",EDGE,"E13.0");var subQ2=makeQuery(id+"F0.imprint","INTERSECT",VERTEX,{"derivedFrom":[subQ1,subQ0]});Q42=makeQuery(id+"F0.imprint","IMPRINT",FACE,{"disambiguationData":[TD([[makeQuery(id+"F0.imprint","IMPRINT",EDGE,{"disambiguationData":[TD([[subQ2,-1.0]])],"derivedFrom":subQ1}),1.0]])]});}
            var Q43;
            {var subQ0=sQuery(id+"F0.wireOp",EDGE,"E25.0");var subQ1=sQuery(id+"F0.wireOp",EDGE,"E15.0");var subQ2=makeQuery(id+"F0.imprint","INTERSECT",VERTEX,{"derivedFrom":[subQ1,subQ0]});Q43=makeQuery(id+"F0.imprint","IMPRINT",FACE,{"disambiguationData":[TD([[makeQuery(id+"F0.imprint","IMPRINT",EDGE,{"disambiguationData":[TD([[subQ2,-1.0]])],"derivedFrom":subQ1}),1.0]])]});}
            var Q44;
            {var subQ0=sQuery(id+"F0.wireOp",EDGE,"E25.0");var subQ1=sQuery(id+"F0.wireOp",EDGE,"E2");var subQ2=makeQuery(id+"F0.imprint","INTERSECT",VERTEX,{"derivedFrom":[subQ1,subQ0]});Q44=makeQuery(id+"F0.imprint","IMPRINT",FACE,{"disambiguationData":[TD([[makeQuery(id+"F0.imprint","IMPRINT",EDGE,{"disambiguationData":[TD([[subQ2,-1.0]])],"derivedFrom":subQ1}),-1.0]])]});}
            var Q45;
            {var subQ0=sQuery(id+"F0.wireOp",EDGE,"E16.0");var subQ1=sQuery(id+"F0.wireOp",EDGE,"E4");var subQ2=makeQuery(id+"F0.imprint","INTERSECT",VERTEX,{"derivedFrom":[subQ1,subQ0]});Q45=makeQuery(id+"F0.imprint","IMPRINT",FACE,{"disambiguationData":[TD([[makeQuery(id+"F0.imprint","IMPRINT",EDGE,{"disambiguationData":[TD([[subQ2,-1.0]])],"derivedFrom":subQ1}),1.0]])]});}
            var Q46;
            {var subQ0=sQuery(id+"F0.wireOp",EDGE,"E14.0");var subQ1=sQuery(id+"F0.wireOp",EDGE,"E4");var subQ2=makeQuery(id+"F0.imprint","INTERSECT",VERTEX,{"derivedFrom":[subQ1,subQ0]});Q46=makeQuery(id+"F0.imprint","IMPRINT",FACE,{"disambiguationData":[TD([[makeQuery(id+"F0.imprint","IMPRINT",EDGE,{"disambiguationData":[TD([[subQ2,-1.0]])],"derivedFrom":subQ1}),1.0]])]});}
            var Q47;
            {var subQ0=sQuery(id+"F0.wireOp",EDGE,"E12.0");var subQ1=sQuery(id+"F0.wireOp",EDGE,"E4");var subQ2=makeQuery(id+"F0.imprint","INTERSECT",VERTEX,{"derivedFrom":[subQ1,subQ0]});Q47=makeQuery(id+"F0.imprint","IMPRINT",FACE,{"disambiguationData":[TD([[makeQuery(id+"F0.imprint","IMPRINT",EDGE,{"disambiguationData":[TD([[subQ2,-1.0]])],"derivedFrom":subQ1}),1.0]])]});}
            var Q48;
            {var subQ0=sQuery(id+"F0.wireOp",EDGE,"E10.0");var subQ1=sQuery(id+"F0.wireOp",EDGE,"E4");var subQ2=makeQuery(id+"F0.imprint","INTERSECT",VERTEX,{"derivedFrom":[subQ1,subQ0]});Q48=makeQuery(id+"F0.imprint","IMPRINT",FACE,{"disambiguationData":[TD([[makeQuery(id+"F0.imprint","IMPRINT",EDGE,{"disambiguationData":[TD([[subQ2,-1.0]])],"derivedFrom":subQ1}),1.0]])]});}
            var Q49;
            {var subQ0=sQuery(id+"F0.wireOp",EDGE,"E4");var subQ5=sQuery(id+"F0.wireOp",EDGE,"E9.0");var subQ7=makeQuery(id+"F0.imprint","INTERSECT",VERTEX,{"derivedFrom":[subQ0,subQ5]});Q49=makeQuery(id+"F0.imprint","IMPRINT",FACE,{"disambiguationData":[TD([[makeQuery(id+"F0.imprint","IMPRINT",EDGE,{"disambiguationData":[TD([[subQ7,1.0]])],"derivedFrom":subQ5}),-1.0]])]});}
            extrude(context, id + "F5", {"entities" : qUnion([Q0, Q1, Q2, Q3, Q4, Q5, Q6, Q7, Q8, Q9, Q10, Q11, Q12, Q13, Q14, Q15, Q16, Q17, Q18, Q19, Q20, Q21, Q22, Q23, Q24, Q25, Q26, Q27, Q28, Q29, Q30, Q31, Q32, Q33, Q34, Q35, Q36, Q37, Q38, Q39, Q40, Q41, Q42, Q43, Q44, Q45, Q46, Q47, Q48, Q49]), "depth" : 25.4 * mm, "offsetDistance" : 25.4 * mm});
        }
    });
